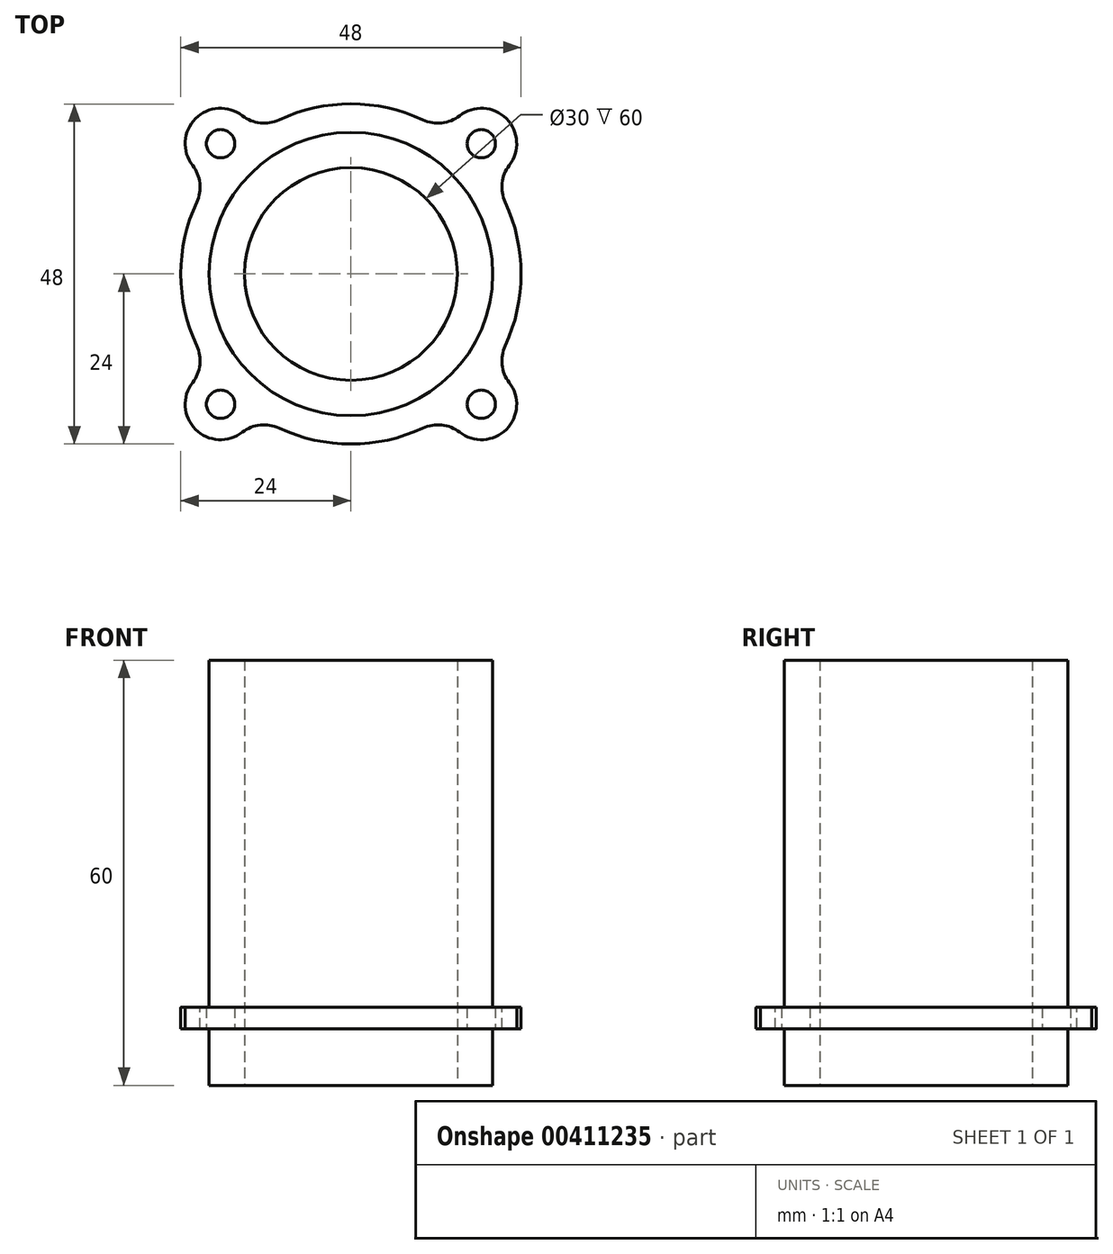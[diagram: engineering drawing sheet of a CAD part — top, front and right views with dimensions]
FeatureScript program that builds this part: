
annotation { "Feature Type Name" : "Feature", "Feature Type Description" : "" }
export const myFeature = defineFeature(function(context is Context, id is Id, definition is map)
    precondition{}
    {
        {
            var Q0;
            Q0=qCreatedBy(makeId("Top.planeOp"),FACE);
            var sketch = newSketch(context, id + "F0", { "sketchPlane" : qUnion([Q0])});
            skCircle(sketch, "E0", {"center": v(0, 0) * mm, "radius": 20 * mm});
            skCircle(sketch, "E1", {"center": v(0, 0) * mm, "radius": 26 * mm, "construction": true});
            skArc(sketch, "E2", {"start": v(-19.79, 13.58) * mm, "mid": v(-24, 0) * mm, "end": v(-19.79, -13.58) * mm});
            skCircle(sketch, "E3", {"center": v(-18.38, 18.38) * mm, "radius": 2 * mm});
            skCircle(sketch, "E4", {"center": v(18.38, 18.38) * mm, "radius": 2 * mm});
            skCircle(sketch, "E5", {"center": v(18.38, -18.38) * mm, "radius": 2 * mm});
            skCircle(sketch, "E6", {"center": v(-18.38, -18.38) * mm, "radius": 2 * mm});
            skArc(sketch, "E7", {"start": v(-13.58, 19.79) * mm, "mid": v(-21.92, 21.92) * mm, "end": v(-19.79, 13.58) * mm});
            skArc(sketch, "E8", {"start": v(19.79, 13.58) * mm, "mid": v(21.92, 21.92) * mm, "end": v(13.58, 19.79) * mm});
            skArc(sketch, "E9", {"start": v(13.58, -19.79) * mm, "mid": v(21.92, -21.92) * mm, "end": v(19.79, -13.58) * mm});
            skArc(sketch, "E10", {"start": v(-19.79, -13.58) * mm, "mid": v(-21.92, -21.92) * mm, "end": v(-13.58, -19.79) * mm});
            skArc(sketch, "E11.trimOffspring", {"start": v(13.58, 19.79) * mm, "mid": v(0, 24) * mm, "end": v(-13.58, 19.79) * mm});
            skArc(sketch, "E12.trimOffspring", {"start": v(19.79, -13.58) * mm, "mid": v(24, 0) * mm, "end": v(19.79, 13.58) * mm});
            skArc(sketch, "E13.trimOffspring", {"start": v(-13.58, -19.79) * mm, "mid": v(0, -24) * mm, "end": v(13.58, -19.79) * mm});
            skLineSegment(sketch, "E14", {"start": v(-18.38, 18.38) * mm, "end": v(18.38, -18.38) * mm, "construction": true});
            skLineSegment(sketch, "E15", {"start": v(18.38, 18.38) * mm, "end": v(-18.38, -18.38) * mm, "construction": true});
            skSolve(sketch);
        }
        {
            var Q0;
            Q0 = qSketchRegion(id + "F0", true);
            extrude(context, id + "F1", {"entities" : qUnion([Q0]), "depth" : 3 * mm});
        }
        {
            var Q0;
            Q0=makeQuery(id+"F1.opExtrude","SWEPT_EDGE",EDGE,{"disambiguationData":[OSD([sQuery(id+"F0.wireOp",EDGE,"E10"),sQuery(id+"F0.wireOp",EDGE,"E13.trimOffspring")])]});
            var Q1;
            Q1=makeQuery(id+"F1.opExtrude","SWEPT_EDGE",EDGE,{"disambiguationData":[OSD([sQuery(id+"F0.wireOp",EDGE,"E8"),sQuery(id+"F0.wireOp",EDGE,"E12.trimOffspring")])]});
            var Q2;
            Q2=makeQuery(id+"F1.opExtrude","SWEPT_EDGE",EDGE,{"disambiguationData":[OSD([sQuery(id+"F0.wireOp",EDGE,"E2"),sQuery(id+"F0.wireOp",EDGE,"E7")])]});
            var Q3;
            Q3=makeQuery(id+"F1.opExtrude","SWEPT_EDGE",EDGE,{"disambiguationData":[OSD([sQuery(id+"F0.wireOp",EDGE,"E2"),sQuery(id+"F0.wireOp",EDGE,"E10")])]});
            var Q4;
            Q4=makeQuery(id+"F1.opExtrude","SWEPT_EDGE",EDGE,{"disambiguationData":[OSD([sQuery(id+"F0.wireOp",EDGE,"E9"),sQuery(id+"F0.wireOp",EDGE,"E12.trimOffspring")])]});
            var Q5;
            Q5=makeQuery(id+"F1.opExtrude","SWEPT_EDGE",EDGE,{"disambiguationData":[OSD([sQuery(id+"F0.wireOp",EDGE,"E7"),sQuery(id+"F0.wireOp",EDGE,"E11.trimOffspring")])]});
            var Q6;
            Q6=makeQuery(id+"F1.opExtrude","SWEPT_EDGE",EDGE,{"disambiguationData":[OSD([sQuery(id+"F0.wireOp",EDGE,"E9"),sQuery(id+"F0.wireOp",EDGE,"E13.trimOffspring")])]});
            var Q7;
            Q7=makeQuery(id+"F1.opExtrude","SWEPT_EDGE",EDGE,{"disambiguationData":[OSD([sQuery(id+"F0.wireOp",EDGE,"E8"),sQuery(id+"F0.wireOp",EDGE,"E11.trimOffspring")])]});
            fillet(context, id + "F2", {"entities" : qUnion([Q0, Q1, Q2, Q3, Q4, Q5, Q6, Q7]), "radius" : 5 * mm, "tangentPropagation" : true, "allowEdgeOverflow" : false});
        }
        {
            var Q0;
            Q0=qCreatedBy(makeId("Top.planeOp"),FACE);
            var sketch = newSketch(context, id + "F3", { "sketchPlane" : qUnion([Q0])});
            skCircle(sketch, "E16", {"center": v(0, 0) * mm, "radius": 15 * mm});
            skCircle(sketch, "E17", {"center": v(0, 0) * mm, "radius": 20 * mm});
            skSolve(sketch);
        }
        {
            var Q0;
            Q0 = qSketchRegion(id + "F3", true);
            extrude(context, id + "F4", {"entities" : qUnion([Q0]), "operationType" : NewBodyOperationType.ADD, "depth" : 52 * mm, "hasSecondDirection" : true, "secondDirectionOppositeDirection" : true, "secondDirectionDepth" : 8 * mm});
        }
    });
